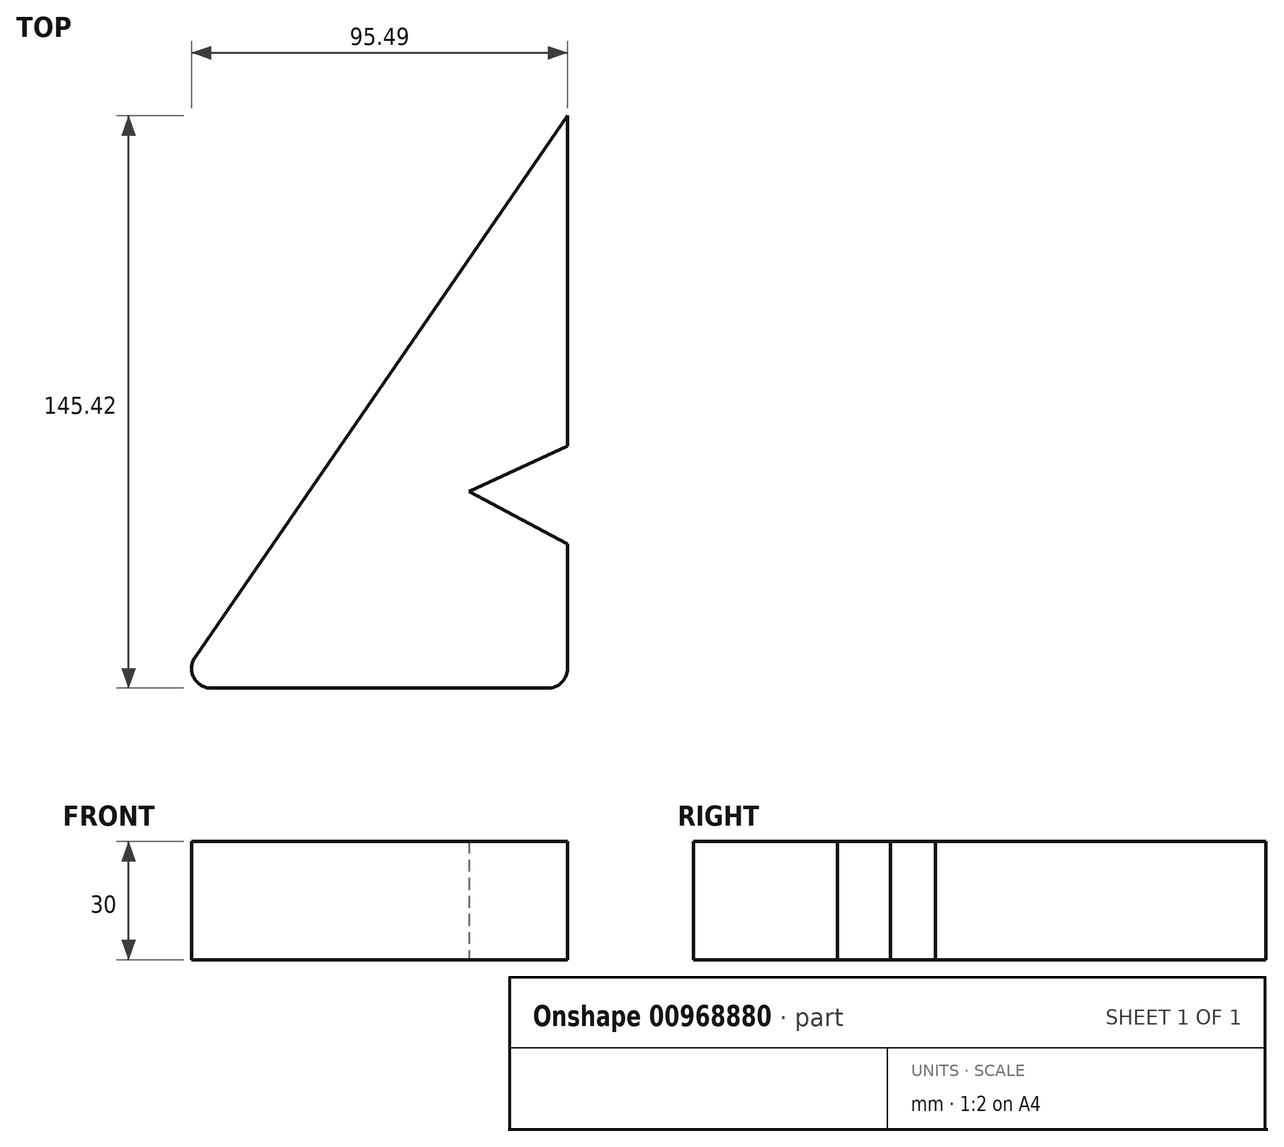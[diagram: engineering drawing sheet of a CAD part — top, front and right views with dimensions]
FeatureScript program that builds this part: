
annotation { "Feature Type Name" : "Feature", "Feature Type Description" : "" }
export const myFeature = defineFeature(function(context is Context, id is Id, definition is map)
    precondition{}
    {
        {
            var Q0;
            Q0=qCreatedBy(makeId("Top.planeOp"),FACE);
            var sketch = newSketch(context, id + "F0", { "sketchPlane" : qUnion([Q0])});
            skLineSegment(sketch, "E0.top", {"start": v(-50, -50) * mm, "end": v(50, -50) * mm});
            skLineSegment(sketch, "E0.right", {"start": v(50, 50) * mm, "end": v(50, 11.46) * mm});
            skPoint(sketch, "E0.middle", {"position": v(0, 0) * mm});
            skLineSegment(sketch, "E1", {"start": v(25, 0) * mm, "end": v(50, -13.4) * mm});
            skLineSegment(sketch, "E2", {"start": v(50, 11.46) * mm, "end": v(25, 0) * mm});
            skPoint(sketch, "E3.orphan", {"position": v(50, 0) * mm});
            skLineSegment(sketch, "E4.trimOffspring", {"start": v(50, -13.4) * mm, "end": v(50, -50) * mm});
            skPoint(sketch, "E0.left.start.orphan", {"position": v(-50, 50) * mm});
            skLineSegment(sketch, "E5", {"start": v(50, 50) * mm, "end": v(50, 95.42) * mm});
            skLineSegment(sketch, "E6", {"start": v(50, 95.42) * mm, "end": v(-50, -50) * mm});
            skSolve(sketch);
        }
        {
            var Q0;
            Q0 = qSketchRegion(id + "F0", true);
            extrude(context, id + "F1", {"entities" : qUnion([Q0]), "depth" : 30 * mm, "offsetDistance" : 25 * mm});
        }
        {
            var Q0;
            Q0=makeQuery(id+"F1.opExtrude","SWEPT_EDGE",EDGE,{"disambiguationData":[OSD([sQuery(id+"F0.wireOp",EDGE,"E0.top"),sQuery(id+"F0.wireOp",EDGE,"E4.trimOffspring")])]});
            var Q1;
            Q1=makeQuery(id+"F1.opExtrude","SWEPT_EDGE",EDGE,{"disambiguationData":[OSD([sQuery(id+"F0.wireOp",EDGE,"E0.top"),sQuery(id+"F0.wireOp",EDGE,"E6")])]});
            fillet(context, id + "F2", {"entities" : qUnion([Q0, Q1]), "radius" : 5 * mm, "tangentPropagation" : true, "allowEdgeOverflow" : false});
        }
    });
